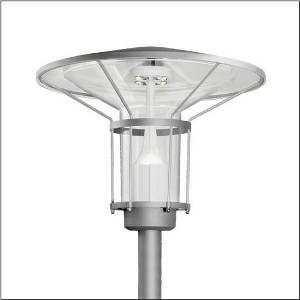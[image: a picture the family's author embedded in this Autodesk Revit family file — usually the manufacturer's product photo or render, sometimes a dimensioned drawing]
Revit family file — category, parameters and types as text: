
# Revit family: laterne_classic_iq___p1_0a_5xa5245nf14h_cdb6
name_source: partatom
category: Lighting Fixtures
units: mm (PartAtom-declared; Revit-internal decimal feet)

## family parameters
Cut with Voids When Loaded = No
Host = Face
Light Source = No
Part Type = Normal
Room Calculation Point = No
Round Connector Dimension = Use Diameter
Shared = No

## types (1)
- --- (1 x LED, 1360 lm, 11.8 W, 2700K)
    Apparent Load = 12 VA
    CIE Flux Codes = 30 61 91 96 100
    Color Rendering = 70
    Color Temperature = 2700K
    Default Elevation = 1800 mm
    Description = Lantern Classic iQ, mast luminaire, Module 540 iQ-SR, primary light control with 3 zone facetted reflector, of plastic, silver coated, highly specular, structured, primary optical cover: cover, of PMMA, transparent, light distribution: P1.0a, light emission: direct distribution, primary light characteristic: strongly asymmetric, installation type: post-top, LED, High Power LED, rated luminous flux: 1.360lm, luminous efficacy: 115lm/W, light colour: 727, colour temperature: 2700K, control gear: iQ Street-Remote, control: pre-setting: logarithmic dimming characteristic, Street-Remote, Auto-Match, Temp-Guard, Lumen-Switch, Night-Set, Smart-Wire, Light-Fading, Desk-Remote (wireless, voltage-free reading and setting of iQ features in the workshop via application-optimized NFC function/RFID function), optimised constant luminous flux control (CLO 2.0), with terminal, 6-pole, max. 2.5mm², mains connection: 230..240V, AC, 50/60Hz, start of lifetime: 12W, end of service life: 12W, reduction: 5W, luminaire housing, upper part, of glass-fibre reinforced polyester, coated, Siteco® metallic grey (DB 702S), diameter: 750mm, height: 596mm, spigot size: d x l = 76 x 70mm (post-top) | with reducer (optional accessory) 60 x 70mm, mounting height: 3..5m, post-top mast mounting element, of diecast aluminium, coated, Siteco® metallic grey (DB 702S), Module 540 iQ-SR, traffic white (RAL 9016), equipment: standard, protection rating (complete): IP65, insulation class (complete): insulation class II (safety insulation), certification: CE, ENEC, VDE, packaging unit: 1 piece

Light Distribution: P1.0a
    Height = 596 mm
    Lamp = 1 x LED
    Lamp Light Flux = 1360 lm
    Lamp Power = 11.8 W
    Lamp count = 1
    Length = 750 mm
    Luminous efficacy = 115 lm/W
    Manufacturer = Siteco
    ModVariant = No
    Model = 5XA5245NF14H
    Number of Poles = 1
    OnlyDefault = Yes
    Power Factor = 1
    Product Name = Laterne Classic iQ | P1.0a
    Product group = mast luminaire | pylon top
    ProductGroupID = 6100
    Protection Class = Protection class II
    Protection Degree = IP 65
    RLX_Detail_Level = 1
    RLX_Emergency_Light_Flux = 0 lm
    RLX_Emergency_Type = 0
    RLX_Emergency_Type_DB = No
    RlxData = <blob elided: 93969 chars, md5=06218d24>
    Socket = socket
    Standby Power = 0 W
    System Light Flux = 1360 lm
    System Power = 12 W
    Type Comments = factory setting: luminous flux: 100 % | dim-lin: 254 | 472 mA
    Type Image = l_1006052.jpg
    URL = http://relux.com
    VarID = @adj_174791
    Voltage = 0 V
    Weight = 0.00 kg
    Width = 0 mm  [stored 0 ft]

note: [stored X ft] marks values corroborated as IEEE doubles in the binary element streams (Revit-internal decimal feet)

## geometry (parser evidence)
native form markers: Blend x4, Sweep x11
no freeform markers — native parametric forms only
